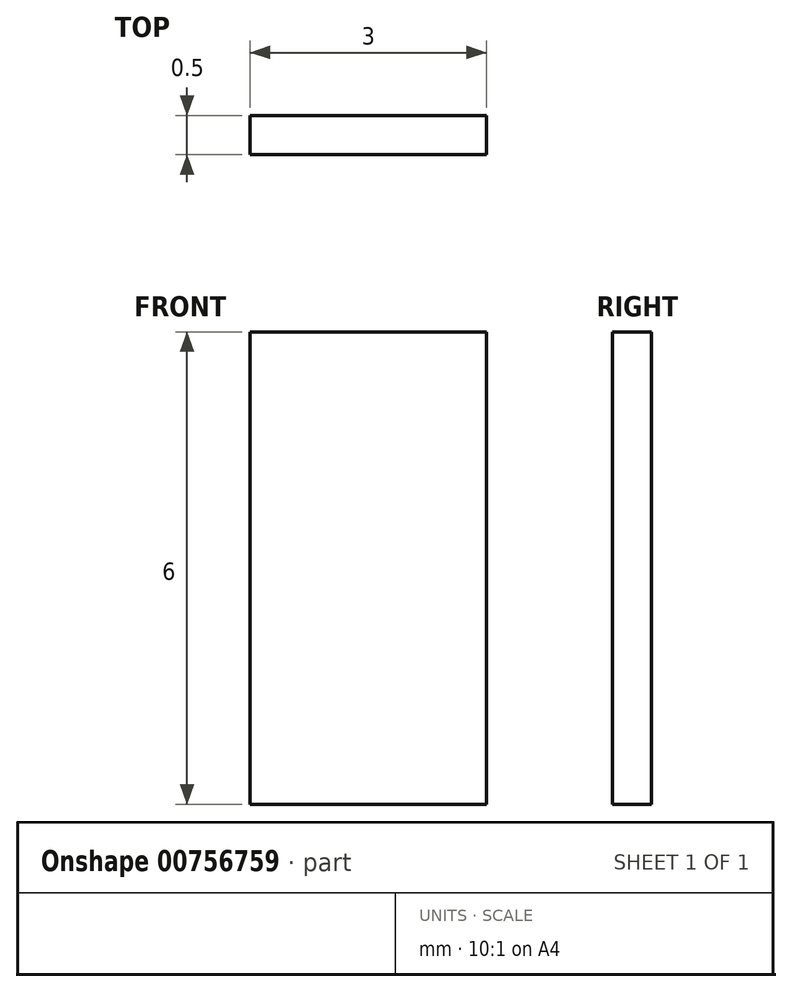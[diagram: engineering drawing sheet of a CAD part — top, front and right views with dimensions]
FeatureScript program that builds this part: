
annotation { "Feature Type Name" : "Feature", "Feature Type Description" : "" }
export const myFeature = defineFeature(function(context is Context, id is Id, definition is map)
    precondition{}
    {
        {
            var Q0;
            Q0=qCreatedBy(makeId("Top.planeOp"),FACE);
            var sketch = newSketch(context, id + "F0", { "sketchPlane" : qUnion([Q0])});
            skLineSegment(sketch, "E0.bottom", {"start": v(1.5, 0.25) * mm, "end": v(-1.5, 0.25) * mm});
            skLineSegment(sketch, "E0.top", {"start": v(1.5, -0.25) * mm, "end": v(-1.5, -0.25) * mm});
            skLineSegment(sketch, "E0.left", {"start": v(1.5, 0.25) * mm, "end": v(1.5, -0.25) * mm});
            skLineSegment(sketch, "E0.right", {"start": v(-1.5, 0.25) * mm, "end": v(-1.5, -0.25) * mm});
            skPoint(sketch, "E0.middle", {"position": v(0, 0) * mm});
            skSolve(sketch);
        }
        {
            var Q0;
            Q0 = qSketchRegion(id + "F0", true);
            extrude(context, id + "F1", {"entities" : qUnion([Q0]), "depth" : 6 * mm, "offsetDistance" : 25 * mm});
        }
    });
